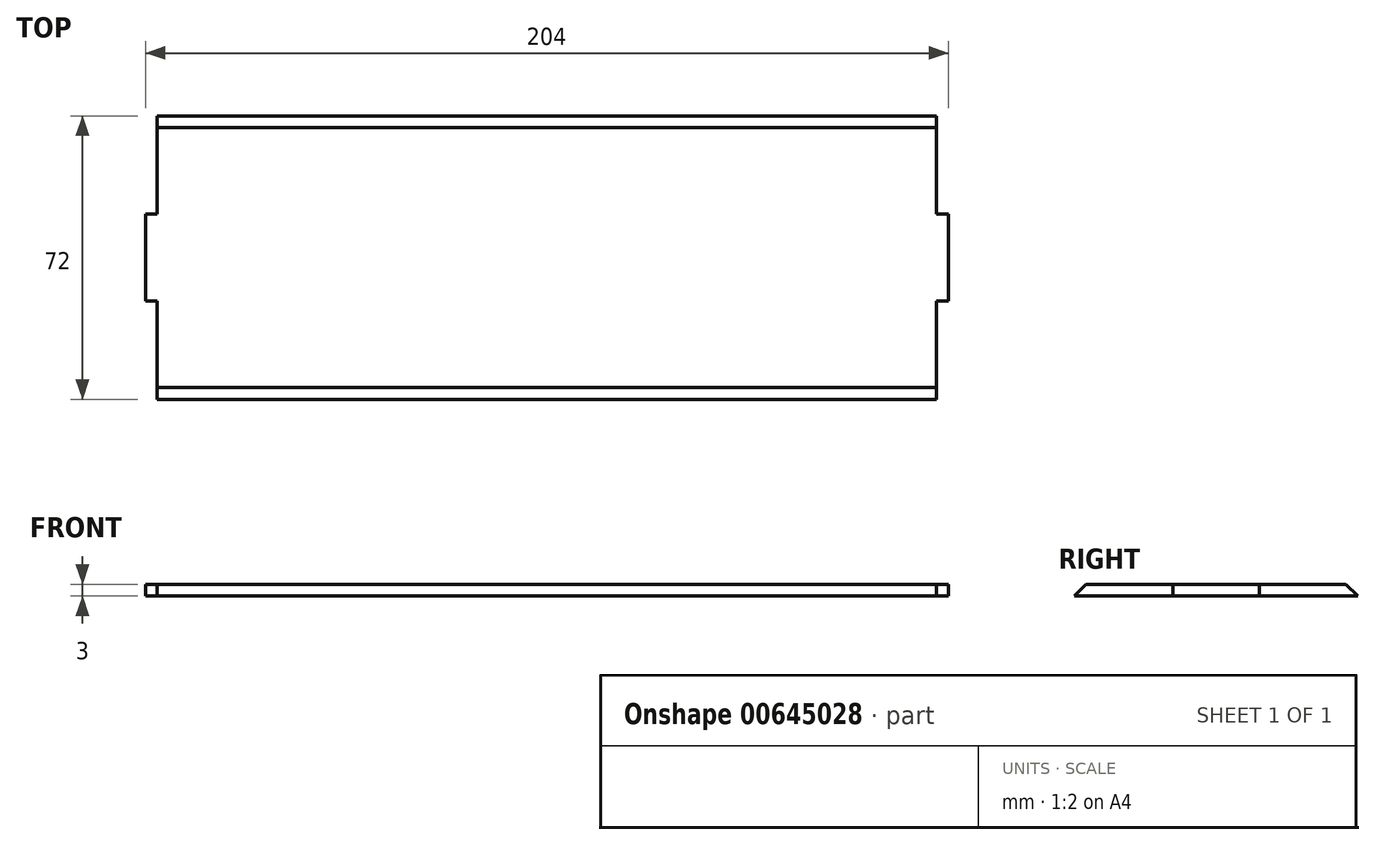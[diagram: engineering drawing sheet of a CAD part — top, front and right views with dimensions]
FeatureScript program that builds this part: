
annotation { "Feature Type Name" : "Feature", "Feature Type Description" : "" }
export const myFeature = defineFeature(function(context is Context, id is Id, definition is map)
    precondition{}
    {
        {
            var Q0;
            Q0=qCreatedBy(makeId("Top.planeOp"),FACE);
            var sketch = newSketch(context, id + "F0", { "sketchPlane" : qUnion([Q0])});
            skLineSegment(sketch, "E0", {"start": v(-82.15, 0) * mm, "end": v(-82.15, 72) * mm});
            skLineSegment(sketch, "E1", {"start": v(-82.15, 72) * mm, "end": v(121.85, 72) * mm});
            skLineSegment(sketch, "E2", {"start": v(121.85, 72) * mm, "end": v(121.85, 0) * mm});
            skLineSegment(sketch, "E3", {"start": v(121.85, 0) * mm, "end": v(-82.15, 0) * mm});
            skLineSegment(sketch, "E4", {"start": v(-79.15, 72) * mm, "end": v(-79.15, 0) * mm});
            skLineSegment(sketch, "E5", {"start": v(118.85, 72) * mm, "end": v(118.85, 0) * mm});
            skLineSegment(sketch, "E6", {"start": v(-82.15, 47) * mm, "end": v(-79.15, 47) * mm});
            skLineSegment(sketch, "E7", {"start": v(-82.15, 25) * mm, "end": v(-79.15, 25) * mm});
            skLineSegment(sketch, "E8", {"start": v(118.85, 47) * mm, "end": v(121.85, 47) * mm});
            skLineSegment(sketch, "E9", {"start": v(118.85, 25) * mm, "end": v(121.85, 25) * mm});
            skSolve(sketch);
        }
        {
            var Q0;
            {var subQ0=sQuery(id+"F0.wireOp",EDGE,"E4");var subQ3=sQuery(id+"F0.wireOp",EDGE,"E1");var subQ4=makeQuery(id+"F0.imprint","INTERSECT",VERTEX,{"derivedFrom":[subQ3,subQ0]});Q0=makeQuery(id+"F0.imprint","IMPRINT",FACE,{"disambiguationData":[TD([[makeQuery(id+"F0.imprint","IMPRINT",EDGE,{"disambiguationData":[TD([[subQ4,-1.0]])],"derivedFrom":subQ3}),-1.0]])]});}
            var Q1;
            {var subQ0=sQuery(id+"F0.wireOp",EDGE,"E8");Q1=makeQuery(id+"F0.imprint","IMPRINT",FACE,{"disambiguationData":[TD([[makeQuery(id+"F0.imprint","IMPRINT",EDGE,{"derivedFrom":subQ0}),-1.0]])]});}
            var Q2;
            {var subQ0=sQuery(id+"F0.wireOp",EDGE,"E6");Q2=makeQuery(id+"F0.imprint","IMPRINT",FACE,{"disambiguationData":[TD([[makeQuery(id+"F0.imprint","IMPRINT",EDGE,{"derivedFrom":subQ0}),-1.0]])]});}
            extrude(context, id + "F1", {"entities" : qUnion([Q0, Q1, Q2]), "depth" : 3 * mm, "offsetDistance" : 25 * mm});
        }
        {
            var Q0;
            Q0=makeQuery(id+"F1.opExtrude","CAP_EDGE",EDGE,{"disambiguationData":[OSD([sQuery(id+"F0.wireOp",EDGE,"E3")])],"isStart":false});
            var Q1;
            Q1=makeQuery(id+"F1.opExtrude","CAP_EDGE",EDGE,{"disambiguationData":[OSD([sQuery(id+"F0.wireOp",EDGE,"E1")])],"isStart":false});
            chamfer(context, id + "F2", {"entities" : qUnion([Q0, Q1]), "width" : 3 * mm, "tangentPropagation" : true});
        }
    });
